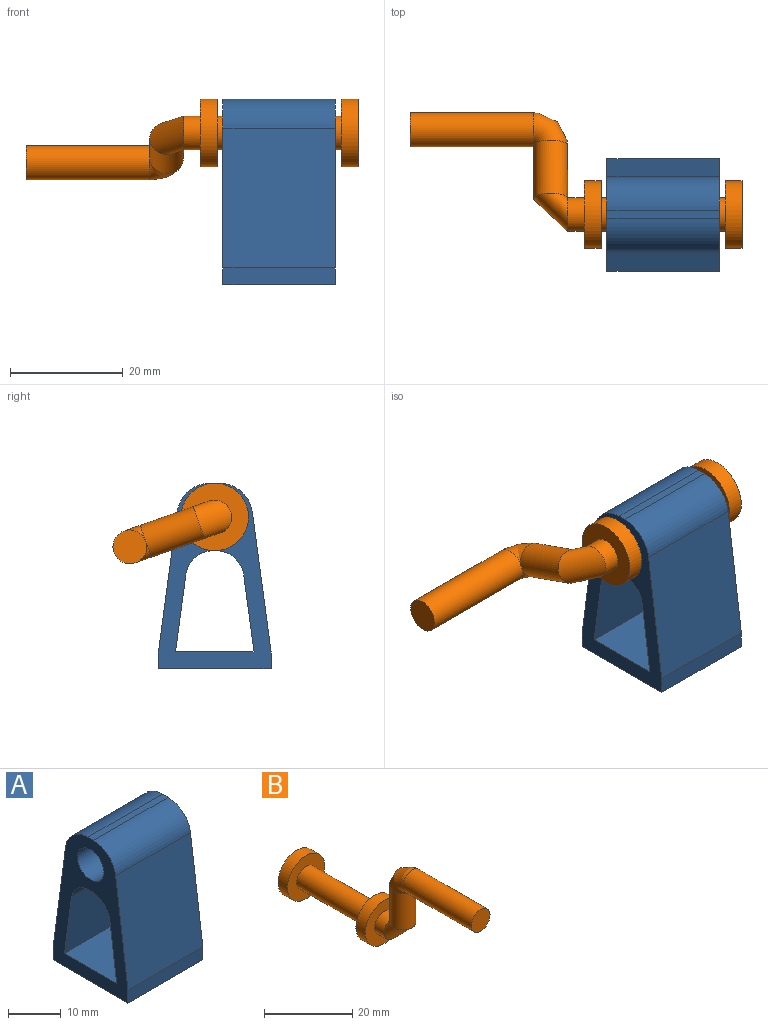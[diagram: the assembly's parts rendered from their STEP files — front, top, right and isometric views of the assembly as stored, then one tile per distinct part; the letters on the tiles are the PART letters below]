
ASSEMBLY  parts=2 mates=1
PART A: 17 faces, bbox 20x20x33 mm
  f0: plane 33x20mm, normal (-1,0,0), area 290.2mm2, adj f1,f3,f4,f5,f6,f7,f8,f9
  f1: plane 20x20mm, normal (0,0,-1), area 400mm2, adj f0,f2,f3,f4
  f2: plane 33x20mm, normal (1,0,0), area 290.2mm2, adj f1,f3,f4,f5,f6,f7,f8,f9
  f3: plane 20x3mm, normal (0,-1,0), area 60mm2, adj f0,f1,f2,f7
  f4: plane 20x3mm, normal (0,1,0), area 60mm2, adj f0,f1,f2,f5
  f5: plane 24.79x20mm, normal (0,0.99,0.13), area 500.2mm2, adj f0,f2,f4,f13
  f6: plane 20x1.49mm, normal (0,0,1), area 29.9mm2, adj f0,f2,f13,f14
  f7: plane 24.79x20mm, normal (0,-0.99,0.13), area 500.2mm2, adj f0,f2,f3,f14
  f8: plane 20x0.39mm, normal (0,0,-1), area 7.8mm2, adj f0,f2,f15,f16
  f9: plane 20x13.66mm, normal (0,0.99,-0.13), area 275.6mm2, adj f0,f2,f11,f16
  f10: plane 20x13.66mm, normal (0,-0.99,-0.13), area 275.6mm2, adj f0,f2,f11,f15
  f11: plane 20x13.95mm, normal (0,0,1), area 278.9mm2, adj f0,f2,f9,f10
  f12: cylinder r=3.5mm len=20mm, axis (-1,0,0), area 439.8mm2, adj f0,f2
  f13: cylinder r=6mm len=20mm, axis (-1,0,0), area 172.6mm2, adj f0,f2,f5,f6
  f14: cylinder r=6mm len=20mm, axis (-1,0,0), area 172.6mm2, adj f0,f2,f6,f7
  f15: cylinder r=5mm len=20mm, axis (-1,0,0), area 143.8mm2, adj f0,f2,f8,f10
  f16: cylinder r=5mm len=20mm, axis (-1,0,0), area 143.8mm2, adj f0,f2,f8,f9
PART B: 13 faces, bbox 12x59x25.5 mm
  f0: plane 6x6mm, normal (0,-1,0), area 28.3mm2, adj f5
  f1: cylinder r=3mm len=6mm, axis (0,-1,0), area 56.5mm2, adj f2,f7
  f2: torus R=3mm, axis (-1,0,0), area 94.9mm2, adj f1,f3
  f3: cylinder r=3mm len=10mm, axis (0,0,1), area 188.5mm2, adj f2,f4
  f4: torus R=3mm, axis (1,0,0), area 88.8mm2, adj f3,f5
  f5: cylinder r=3mm len=22mm, axis (0,-1,0), area 414.7mm2, adj f0,f4
  f6: cylinder r=6mm len=12mm, axis (0,1,0), area 113.1mm2, adj f7,f8
  f7: plane 12x12mm, normal (0,-1,0), area 84.8mm2, adj f1,f6
  f8: plane 12x12mm, normal (0,1,0), area 84.8mm2, adj f6,f12
  f9: plane 12x12mm, normal (0,1,0), area 113.1mm2, adj f10
  f10: cylinder r=6mm len=12mm, axis (0,1,0), area 113.1mm2, adj f9,f11
  f11: plane 12x12mm, normal (0,-1,0), area 84.8mm2, adj f10,f12
  f12: cylinder r=3mm len=22mm, axis (0,-1,0), area 414.7mm2, adj f8,f11
PLACE A at identity fixed
PLACE B rot(axis=(-0.63,-0.63,-0.45),131.8deg) t=(24,0,27)mm
MATE revolute B.f1 <-> A.f12  axis (-1,0,0) through (10,0,27)mm
